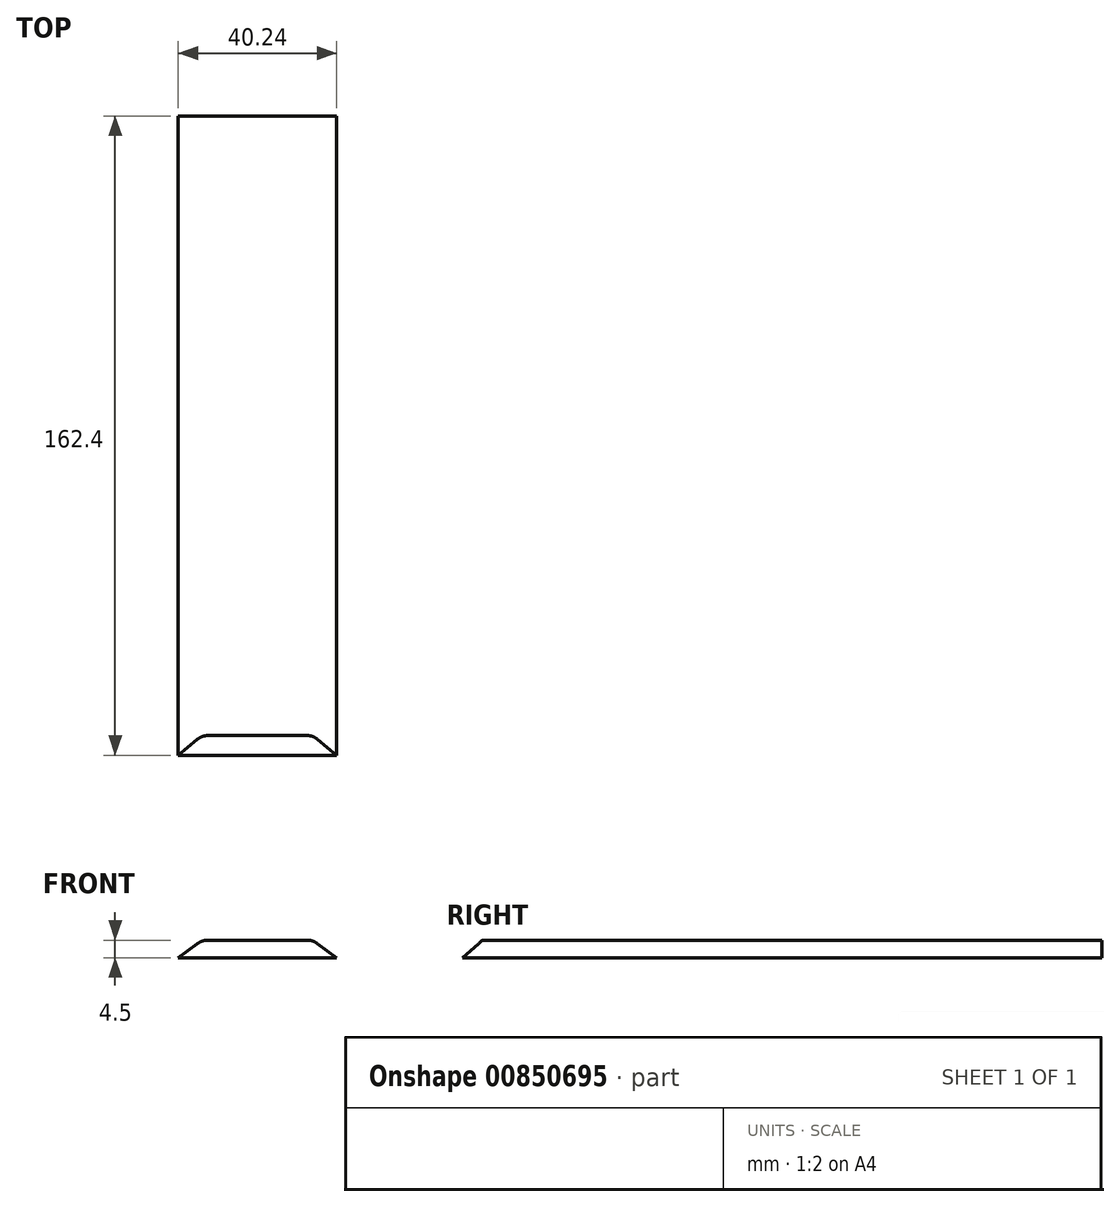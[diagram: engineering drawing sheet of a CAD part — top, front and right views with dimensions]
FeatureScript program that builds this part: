
annotation { "Feature Type Name" : "Feature", "Feature Type Description" : "" }
export const myFeature = defineFeature(function(context is Context, id is Id, definition is map)
    precondition{}
    {
        {
            var Q0;
            Q0=qCreatedBy(makeId("Top.planeOp"),FACE);
            var sketch = newSketch(context, id + "F0", { "sketchPlane" : qUnion([Q0])});
            skLineSegment(sketch, "E0.bottom", {"start": v(3.8, -76.2) * mm, "end": v(-3.81, -76.2) * mm});
            skLineSegment(sketch, "E0.top", {"start": v(3.8, 76.2) * mm, "end": v(-3.81, 76.2) * mm});
            skLineSegment(sketch, "E0.left", {"start": v(3.8, -76.2) * mm, "end": v(3.8, 76.2) * mm});
            skLineSegment(sketch, "E0.right", {"start": v(-3.81, -76.2) * mm, "end": v(-3.81, 76.2) * mm});
            skPoint(sketch, "E0.middle", {"position": v(0, 0) * mm});
            skLineSegment(sketch, "E1.bottom", {"start": v(16.43, -76.2) * mm, "end": v(8.8, -76.2) * mm});
            skLineSegment(sketch, "E1.top", {"start": v(16.43, 76.2) * mm, "end": v(8.81, 76.2) * mm});
            skLineSegment(sketch, "E1.left", {"start": v(16.43, -76.2) * mm, "end": v(16.43, 76.2) * mm});
            skLineSegment(sketch, "E1.right", {"start": v(8.8, -76.2) * mm, "end": v(8.81, 76.2) * mm});
            skPoint(sketch, "E1.middle", {"position": v(12.62, 0) * mm});
            skLineSegment(sketch, "E2.bottom", {"start": v(-8.81, -76.2) * mm, "end": v(-16.43, -76.2) * mm});
            skLineSegment(sketch, "E2.top", {"start": v(-8.8, 76.2) * mm, "end": v(-16.43, 76.2) * mm});
            skLineSegment(sketch, "E2.left", {"start": v(-8.81, -76.2) * mm, "end": v(-8.8, 76.2) * mm});
            skLineSegment(sketch, "E2.right", {"start": v(-16.43, -76.2) * mm, "end": v(-16.43, 76.2) * mm});
            skPoint(sketch, "E2.middle", {"position": v(-12.62, 0) * mm});
            skSolve(sketch);
        }
        {
            var Q0;
            Q0=qCreatedBy(makeId("Front.planeOp"),FACE);
            cPlane(context, id + "F1", {"entities" : qUnion([Q0]), "cplaneType" : CPlaneType.OFFSET, "offset" : 76.2 * mm, "width" : 150 * mm, "height" : 150 * mm});
        }
        {
            var Q0;
            Q0=qCreatedBy(id+"F1.planeOp",FACE);
            var sketch = newSketch(context, id + "F2", { "sketchPlane" : qUnion([Q0])});
            skCircle(sketch, "E3", {"center": v(0, 0) * mm, "radius": 4.5 * mm});
            skCircle(sketch, "E4", {"center": v(12.62, 0) * mm, "radius": 4.5 * mm});
            skCircle(sketch, "E5", {"center": v(-12.62, 0) * mm, "radius": 4.5 * mm});
            skLineSegment(sketch, "E6", {"start": v(-12.62, 0) * mm, "end": v(-12.62, 4.5) * mm});
            skLineSegment(sketch, "E7", {"start": v(0, 0) * mm, "end": v(0, 4.5) * mm});
            skLineSegment(sketch, "E8", {"start": v(12.62, 0) * mm, "end": v(12.62, 4.5) * mm});
            skLineSegment(sketch, "E9", {"start": v(12.62, 4.5) * mm, "end": v(-12.62, 4.5) * mm});
            skLineSegment(sketch, "E10", {"start": v(12.62, 0) * mm, "end": v(20.12, 0) * mm});
            skLineSegment(sketch, "E11", {"start": v(-12.62, 0) * mm, "end": v(-20.12, 0) * mm});
            skLineSegment(sketch, "E12", {"start": v(-20.12, 0) * mm, "end": v(-15.32, 3.6) * mm});
            skLineSegment(sketch, "E13", {"start": v(20.12, 0) * mm, "end": v(15.32, 3.6) * mm});
            skLineSegment(sketch, "E14", {"start": v(15.32, 3.6) * mm, "end": v(12.62, 0) * mm});
            skLineSegment(sketch, "E15", {"start": v(20.12, 0) * mm, "end": v(-20.12, 0) * mm});
            skSolve(sketch);
        }
        {
            var Q0;
            {var subQ0=sQuery(id+"F2.wireOp",EDGE,"E13");Q0=makeQuery(id+"F2.imprint","IMPRINT",FACE,{"disambiguationData":[TD([[makeQuery(id+"F2.imprint","IMPRINT",EDGE,{"derivedFrom":subQ0}),1.0]])]});}
            var Q1;
            {var subQ0=sQuery(id+"F2.wireOp",EDGE,"E12");Q1=makeQuery(id+"F2.imprint","IMPRINT",FACE,{"disambiguationData":[TD([[makeQuery(id+"F2.imprint","IMPRINT",EDGE,{"derivedFrom":subQ0}),-1.0]])]});}
            var Q2;
            {var subQ1=sQuery(id+"F2.wireOp",EDGE,"E3");var subQ3=sQuery(id+"F2.wireOp",EDGE,"E15");var subQ4=makeQuery(id+"F2.imprint","INTERSECT",VERTEX,{"disambiguationData":[OD(0.0)],"derivedFrom":[subQ1,subQ3]});Q2=makeQuery(id+"F2.imprint","IMPRINT",FACE,{"disambiguationData":[TD([[makeQuery(id+"F2.imprint","IMPRINT",EDGE,{"disambiguationData":[TD([[subQ4,1.0]])],"derivedFrom":subQ3}),-1.0]])]});}
            var Q3;
            {var subQ1=sQuery(id+"F2.wireOp",EDGE,"E3");var subQ3=sQuery(id+"F2.wireOp",EDGE,"E15");var subQ4=makeQuery(id+"F2.imprint","INTERSECT",VERTEX,{"disambiguationData":[OD(1.0)],"derivedFrom":[subQ1,subQ3]});Q3=makeQuery(id+"F2.imprint","IMPRINT",FACE,{"disambiguationData":[TD([[makeQuery(id+"F2.imprint","IMPRINT",EDGE,{"disambiguationData":[TD([[subQ4,-1.0]])],"derivedFrom":subQ3}),-1.0]])]});}
            var Q4;
            {var subQ0=sQuery(id+"F2.wireOp",EDGE,"E8");Q4=makeQuery(id+"F2.imprint","IMPRINT",FACE,{"disambiguationData":[TD([[makeQuery(id+"F2.imprint","IMPRINT",EDGE,{"derivedFrom":subQ0}),-1.0]])]});}
            var Q5;
            {var subQ0=sQuery(id+"F2.wireOp",EDGE,"E7");Q5=makeQuery(id+"F2.imprint","IMPRINT",FACE,{"disambiguationData":[TD([[makeQuery(id+"F2.imprint","IMPRINT",EDGE,{"derivedFrom":subQ0}),-1.0]])]});}
            var Q6;
            {var subQ0=sQuery(id+"F2.wireOp",EDGE,"E7");Q6=makeQuery(id+"F2.imprint","IMPRINT",FACE,{"disambiguationData":[TD([[makeQuery(id+"F2.imprint","IMPRINT",EDGE,{"derivedFrom":subQ0}),1.0]])]});}
            var Q7;
            {var subQ0=sQuery(id+"F2.wireOp",EDGE,"E14");Q7=makeQuery(id+"F2.imprint","IMPRINT",FACE,{"disambiguationData":[TD([[makeQuery(id+"F2.imprint","IMPRINT",EDGE,{"derivedFrom":subQ0}),1.0]])]});}
            var Q8;
            {var subQ0=sQuery(id+"F2.wireOp",EDGE,"E8");Q8=makeQuery(id+"F2.imprint","IMPRINT",FACE,{"disambiguationData":[TD([[makeQuery(id+"F2.imprint","IMPRINT",EDGE,{"derivedFrom":subQ0}),1.0]])]});}
            var Q9;
            {var subQ0=sQuery(id+"F2.wireOp",EDGE,"E6");Q9=makeQuery(id+"F2.imprint","IMPRINT",FACE,{"disambiguationData":[TD([[makeQuery(id+"F2.imprint","IMPRINT",EDGE,{"derivedFrom":subQ0}),1.0]])]});}
            var Q10;
            {var subQ0=sQuery(id+"F2.wireOp",EDGE,"E6");Q10=makeQuery(id+"F2.imprint","IMPRINT",FACE,{"disambiguationData":[TD([[makeQuery(id+"F2.imprint","IMPRINT",EDGE,{"derivedFrom":subQ0}),-1.0]])]});}
            extrude(context, id + "F3", {"entities" : qUnion([Q0, Q1, Q2, Q3, Q4, Q5, Q6, Q7, Q8, Q9, Q10]), "oppositeDirection" : true, "depth" : 157.4 * mm, "offsetDistance" : 25 * mm});
        }
        {
            var Q0;
            Q0=makeQuery(id+"F3.opExtrude","CAP_FACE",FACE,{"disambiguationData":[OSD([sQuery(id+"F2.wireOp",EDGE,"E4"),sQuery(id+"F2.wireOp",EDGE,"E5"),sQuery(id+"F2.wireOp",EDGE,"E9"),sQuery(id+"F2.wireOp",EDGE,"E12"),sQuery(id+"F2.wireOp",EDGE,"E13"),sQuery(id+"F2.wireOp",EDGE,"E15")])],"isStart":true});
            extrude(context, id + "F4", {"entities" : qUnion([Q0]), "operationType" : NewBodyOperationType.ADD, "depth" : 5 * mm, "offsetDistance" : 25 * mm});
        }
        {
            var Q0;
            Q0=qCreatedBy(makeId("Right.planeOp"),FACE);
            var sketch = newSketch(context, id + "F5", { "sketchPlane" : qUnion([Q0])});
            skLineSegment(sketch, "E16", {"start": v(-76.2, 0) * mm, "end": v(-76.2, 4.5) * mm});
            skLineSegment(sketch, "E17", {"start": v(-81.2, 0) * mm, "end": v(-76.2, 4.5) * mm});
            skLineSegment(sketch, "E18", {"start": v(-76.2, 4.5) * mm, "end": v(-81.2, 4.5) * mm});
            skLineSegment(sketch, "E19", {"start": v(-81.2, 4.5) * mm, "end": v(-81.2, 0) * mm});
            skSolve(sketch);
        }
        {
            var Q0;
            Q0 = qSketchRegion(id + "F5", true);
            extrude(context, id + "F6", {"entities" : qUnion([Q0]), "operationType" : NewBodyOperationType.REMOVE, "endBound" : BoundingType.SYMMETRIC, "oppositeDirection" : true, "depth" : 200 * mm, "offsetDistance" : 25 * mm});
        }
    });
